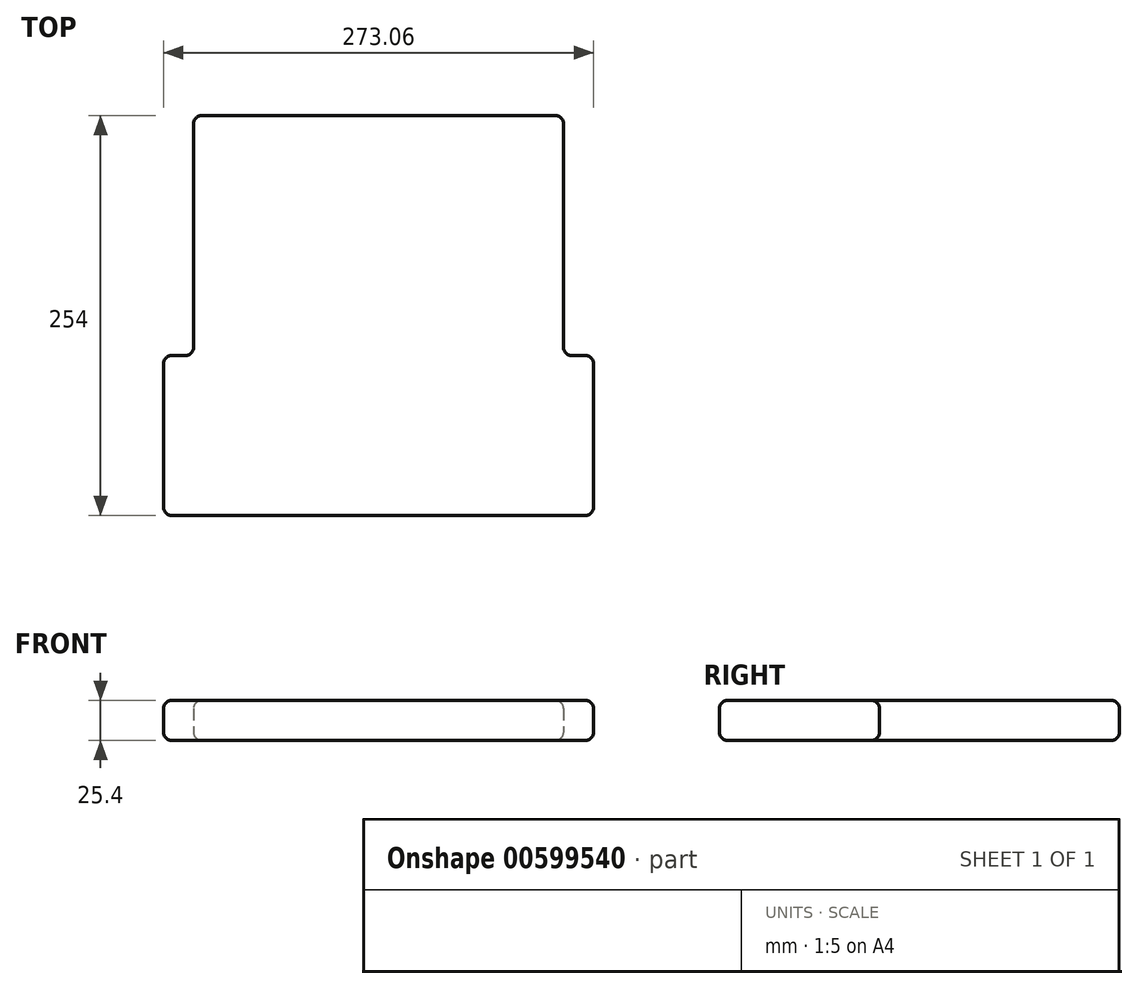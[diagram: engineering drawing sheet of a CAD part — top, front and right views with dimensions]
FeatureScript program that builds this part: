
annotation { "Feature Type Name" : "Feature", "Feature Type Description" : "" }
export const myFeature = defineFeature(function(context is Context, id is Id, definition is map)
    precondition{}
    {
        {
            var Q0;
            Q0=qCreatedBy(makeId("Top.planeOp"),FACE);
            var sketch = newSketch(context, id + "F0", { "sketchPlane" : qUnion([Q0])});
            skLineSegment(sketch, "E0.bottom", {"start": v(-136.53, 127) * mm, "end": v(136.53, 127) * mm});
            skLineSegment(sketch, "E0.top", {"start": v(-136.53, -127) * mm, "end": v(136.53, -127) * mm});
            skLineSegment(sketch, "E0.left", {"start": v(-136.52, 127) * mm, "end": v(-136.53, -127) * mm});
            skLineSegment(sketch, "E0.right", {"start": v(136.53, 127) * mm, "end": v(136.52, -127) * mm});
            skLineSegment(sketch, "E1", {"start": v(0, 127) * mm, "end": v(0, -127) * mm});
            skLineSegment(sketch, "E2", {"start": v(-117.48, 127) * mm, "end": v(-117.48, -25.4) * mm});
            skLineSegment(sketch, "E3", {"start": v(-136.53, -25.4) * mm, "end": v(-117.48, -25.4) * mm});
            skLineSegment(sketch, "E4.MirrorCS", {"start": v(117.48, 127) * mm, "end": v(117.48, -25.4) * mm});
            skLineSegment(sketch, "E5.MirrorCS", {"start": v(136.53, -25.4) * mm, "end": v(117.48, -25.4) * mm});
            skSolve(sketch);
        }
        {
            var Q0;
            {var subQ0=sQuery(id+"F0.wireOp",EDGE,"E1");Q0=makeQuery(id+"F0.imprint","IMPRINT",FACE,{"disambiguationData":[TD([[makeQuery(id+"F0.imprint","IMPRINT",EDGE,{"derivedFrom":subQ0}),-1.0]])]});}
            var Q1;
            {var subQ0=sQuery(id+"F0.wireOp",EDGE,"E1");Q1=makeQuery(id+"F0.imprint","IMPRINT",FACE,{"disambiguationData":[TD([[makeQuery(id+"F0.imprint","IMPRINT",EDGE,{"derivedFrom":subQ0}),1.0]])]});}
            extrude(context, id + "F1", {"entities" : qUnion([Q0, Q1]), "depth" : 25.4 * mm, "offsetDistance" : 25.4 * mm});
        }
        {
            var Q0;
            Q0=makeQuery(id+"F1.opExtrude","CAP_EDGE",EDGE,{"disambiguationData":[OSD([sQuery(id+"F0.wireOp",EDGE,"E0.top")])],"isStart":true});
            var Q1;
            Q1=makeQuery(id+"F1.opExtrude","CAP_EDGE",EDGE,{"disambiguationData":[OSD([sQuery(id+"F0.wireOp",EDGE,"E2")])],"isStart":false});
            var Q2;
            Q2=makeQuery(id+"F1.opExtrude","CAP_EDGE",EDGE,{"disambiguationData":[OSD([sQuery(id+"F0.wireOp",EDGE,"E4.MirrorCS")])],"isStart":true});
            var Q3;
            Q3=makeQuery(id+"F1.opExtrude","CAP_EDGE",EDGE,{"disambiguationData":[OSD([sQuery(id+"F0.wireOp",EDGE,"E0.right")])],"isStart":false});
            var Q4;
            Q4=makeQuery(id+"F1.opExtrude","CAP_EDGE",EDGE,{"disambiguationData":[OSD([sQuery(id+"F0.wireOp",EDGE,"E5.MirrorCS")])],"isStart":false});
            var Q5;
            Q5=makeQuery(id+"F1.opExtrude","SWEPT_EDGE",EDGE,{"disambiguationData":[OSD([sQuery(id+"F0.wireOp",EDGE,"E0.bottom"),sQuery(id+"F0.wireOp",EDGE,"E4.MirrorCS")])]});
            var Q6;
            Q6=makeQuery(id+"F1.opExtrude","CAP_EDGE",EDGE,{"disambiguationData":[OSD([sQuery(id+"F0.wireOp",EDGE,"E0.right")])],"isStart":true});
            var Q7;
            Q7=makeQuery(id+"F1.opExtrude","CAP_EDGE",EDGE,{"disambiguationData":[OSD([sQuery(id+"F0.wireOp",EDGE,"E0.left")])],"isStart":false});
            var Q8;
            Q8=makeQuery(id+"F1.opExtrude","CAP_EDGE",EDGE,{"disambiguationData":[OSD([sQuery(id+"F0.wireOp",EDGE,"E4.MirrorCS")])],"isStart":false});
            var Q9;
            Q9=makeQuery(id+"F1.opExtrude","CAP_EDGE",EDGE,{"disambiguationData":[OSD([sQuery(id+"F0.wireOp",EDGE,"E0.top")])],"isStart":false});
            var Q10;
            Q10=makeQuery(id+"F1.opExtrude","CAP_EDGE",EDGE,{"disambiguationData":[OSD([sQuery(id+"F0.wireOp",EDGE,"E0.bottom")])],"isStart":false});
            var Q11;
            Q11=makeQuery(id+"F1.opExtrude","SWEPT_EDGE",EDGE,{"disambiguationData":[OSD([sQuery(id+"F0.wireOp",EDGE,"E0.right"),sQuery(id+"F0.wireOp",EDGE,"E5.MirrorCS")])]});
            var Q12;
            Q12=makeQuery(id+"F1.opExtrude","CAP_EDGE",EDGE,{"disambiguationData":[OSD([sQuery(id+"F0.wireOp",EDGE,"E3")])],"isStart":true});
            var Q13;
            Q13=makeQuery(id+"F1.opExtrude","CAP_EDGE",EDGE,{"disambiguationData":[OSD([sQuery(id+"F0.wireOp",EDGE,"E3")])],"isStart":false});
            var Q14;
            Q14=makeQuery(id+"F1.opExtrude","SWEPT_EDGE",EDGE,{"disambiguationData":[OSD([sQuery(id+"F0.wireOp",EDGE,"E0.left"),sQuery(id+"F0.wireOp",EDGE,"E3")])]});
            var Q15;
            Q15=makeQuery(id+"F1.opExtrude","CAP_EDGE",EDGE,{"disambiguationData":[OSD([sQuery(id+"F0.wireOp",EDGE,"E2")])],"isStart":true});
            var Q16;
            Q16=makeQuery(id+"F1.opExtrude","CAP_EDGE",EDGE,{"disambiguationData":[OSD([sQuery(id+"F0.wireOp",EDGE,"E0.bottom")])],"isStart":true});
            var Q17;
            Q17=makeQuery(id+"F1.opExtrude","SWEPT_EDGE",EDGE,{"disambiguationData":[OSD([sQuery(id+"F0.wireOp",EDGE,"E0.top"),sQuery(id+"F0.wireOp",EDGE,"E0.left")])]});
            var Q18;
            Q18=makeQuery(id+"F1.opExtrude","SWEPT_EDGE",EDGE,{"disambiguationData":[OSD([sQuery(id+"F0.wireOp",EDGE,"E0.top"),sQuery(id+"F0.wireOp",EDGE,"E0.right")])]});
            var Q19;
            Q19=makeQuery(id+"F1.opExtrude","SWEPT_EDGE",EDGE,{"disambiguationData":[OSD([sQuery(id+"F0.wireOp",EDGE,"E4.MirrorCS"),sQuery(id+"F0.wireOp",EDGE,"E5.MirrorCS")])]});
            var Q20;
            Q20=makeQuery(id+"F1.opExtrude","CAP_EDGE",EDGE,{"disambiguationData":[OSD([sQuery(id+"F0.wireOp",EDGE,"E0.left")])],"isStart":true});
            var Q21;
            Q21=makeQuery(id+"F1.opExtrude","SWEPT_EDGE",EDGE,{"disambiguationData":[OSD([sQuery(id+"F0.wireOp",EDGE,"E2"),sQuery(id+"F0.wireOp",EDGE,"E3")])]});
            var Q22;
            Q22=makeQuery(id+"F1.opExtrude","SWEPT_EDGE",EDGE,{"disambiguationData":[OSD([sQuery(id+"F0.wireOp",EDGE,"E0.bottom"),sQuery(id+"F0.wireOp",EDGE,"E2")])]});
            var Q23;
            Q23=makeQuery(id+"F1.opExtrude","CAP_EDGE",EDGE,{"disambiguationData":[OSD([sQuery(id+"F0.wireOp",EDGE,"E5.MirrorCS")])],"isStart":true});
            fillet(context, id + "F2", {"entities" : qUnion([Q0, Q1, Q2, Q3, Q4, Q5, Q6, Q7, Q8, Q9, Q10, Q11, Q12, Q13, Q14, Q15, Q16, Q17, Q18, Q19, Q20, Q21, Q22, Q23]), "radius" : 5.08 * mm, "tangentPropagation" : true, "allowEdgeOverflow" : false});
        }
    });
